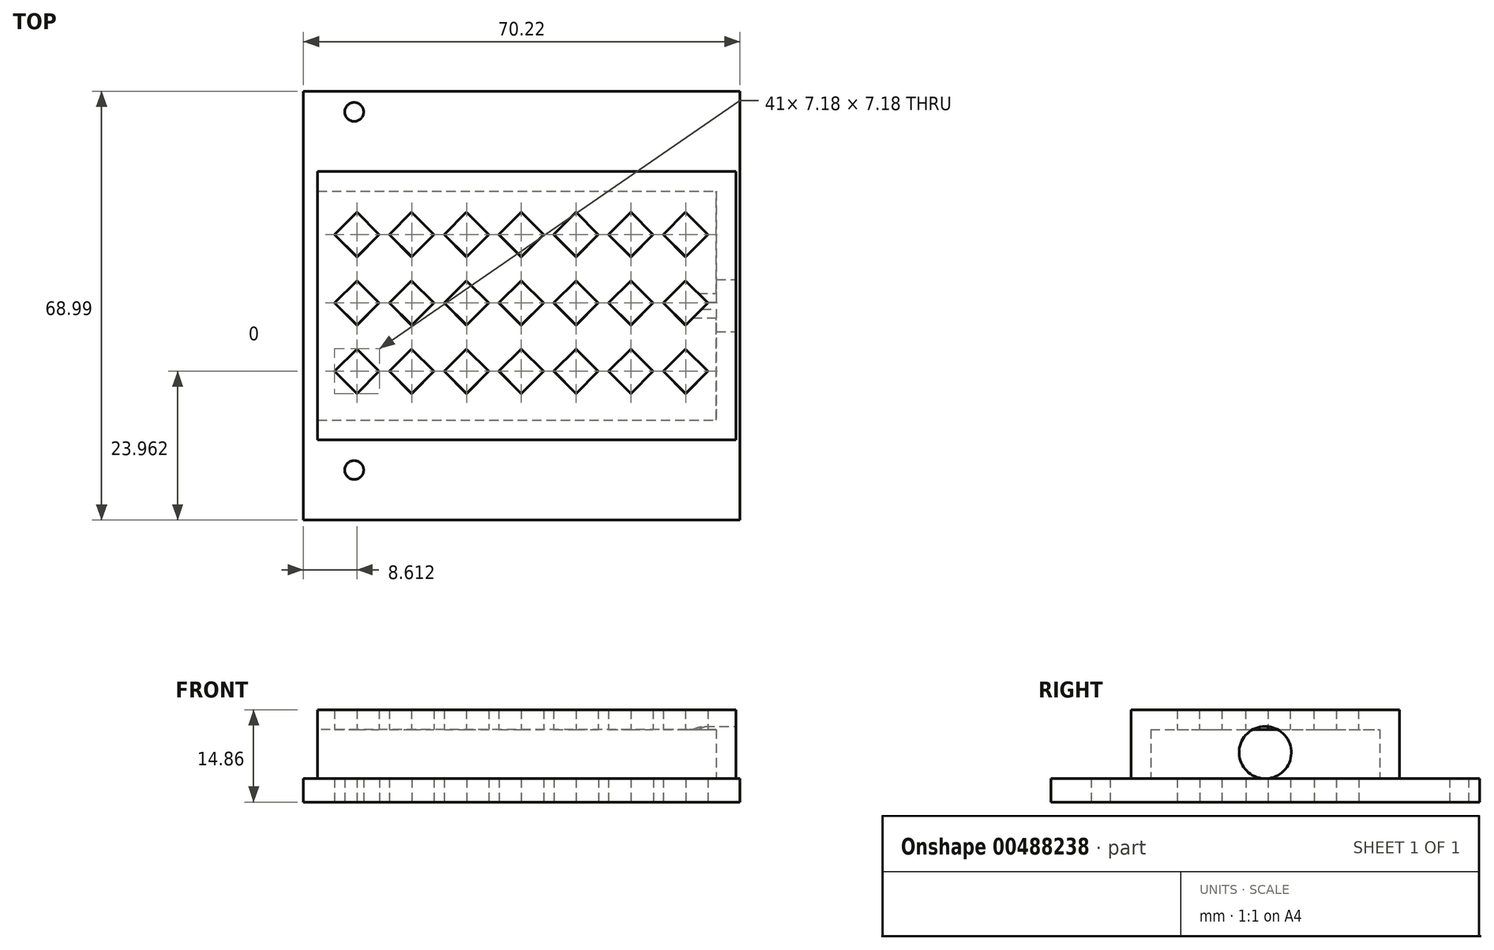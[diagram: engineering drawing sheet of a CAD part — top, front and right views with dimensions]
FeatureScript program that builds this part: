
annotation { "Feature Type Name" : "Feature", "Feature Type Description" : "" }
export const myFeature = defineFeature(function(context is Context, id is Id, definition is map)
    precondition{}
    {
        {
            var Q0;
            Q0=qCreatedBy(makeId("Top.planeOp"),FACE);
            var sketch = newSketch(context, id + "F0", { "sketchPlane" : qUnion([Q0])});
            skLineSegment(sketch, "E0.bottom", {"start": v(-28.53, -73.7) * mm, "end": v(41.7, -73.7) * mm});
            skLineSegment(sketch, "E0.top", {"start": v(-28.53, -4.71) * mm, "end": v(41.7, -4.71) * mm});
            skLineSegment(sketch, "E0.right", {"start": v(41.7, -73.7) * mm, "end": v(41.7, -4.71) * mm});
            skCircle(sketch, "E1", {"center": v(-20.37, -65.65) * mm, "radius": 1.52 * mm});
            skCircle(sketch, "E2.MirrorC", {"center": v(-20.37, -8.04) * mm, "radius": 1.52 * mm});
            skLineSegment(sketch, "E3", {"start": v(-28.53, -73.7) * mm, "end": v(-28.53, -4.71) * mm});
            skPoint(sketch, "E0.left.start.orphan", {"position": v(-40.99, -73.7) * mm});
            skLineSegment(sketch, "E4.bottom", {"start": v(37.9, -57.62) * mm, "end": v(-23.07, -57.62) * mm});
            skLineSegment(sketch, "E4.top", {"start": v(37.9, -20.8) * mm, "end": v(-23.07, -20.8) * mm});
            skLineSegment(sketch, "E4.left", {"start": v(37.9, -57.62) * mm, "end": v(37.9, -20.8) * mm});
            skPoint(sketch, "E4.middle", {"position": v(-28.53, -39.2) * mm});
            skLineSegment(sketch, "E5.0", {"start": v(41.07, -17.62) * mm, "end": v(-26.24, -17.62) * mm});
            skLineSegment(sketch, "E5.1", {"start": v(41.07, -60.8) * mm, "end": v(41.07, -17.62) * mm});
            skLineSegment(sketch, "E5.2", {"start": v(41.07, -60.8) * mm, "end": v(-26.24, -60.8) * mm});
            skLineSegment(sketch, "E5.3", {"start": v(-26.24, -60.8) * mm, "end": v(-26.24, -57.62) * mm});
            skLineSegment(sketch, "E6", {"start": v(-23.07, -20.8) * mm, "end": v(-26.24, -20.8) * mm});
            skLineSegment(sketch, "E7", {"start": v(-23.07, -57.62) * mm, "end": v(-26.24, -57.62) * mm});
            skLineSegment(sketch, "E8.trimOffspring", {"start": v(-26.24, -20.8) * mm, "end": v(-26.24, -17.62) * mm});
            skLineSegment(sketch, "E9.bottom", {"start": v(-19.92, -53.33) * mm, "end": v(-16.33, -49.74) * mm});
            skLineSegment(sketch, "E9.top", {"start": v(-23.5, -49.74) * mm, "end": v(-19.92, -46.15) * mm});
            skLineSegment(sketch, "E9.left", {"start": v(-19.92, -53.33) * mm, "end": v(-23.5, -49.74) * mm});
            skLineSegment(sketch, "E9.right", {"start": v(-16.33, -49.74) * mm, "end": v(-19.92, -46.15) * mm});
            skLineSegment(sketch, "E10.0.1.0", {"start": v(-19.92, -42.33) * mm, "end": v(-23.5, -38.74) * mm});
            skLineSegment(sketch, "E10.0.1.1", {"start": v(-19.92, -42.33) * mm, "end": v(-16.33, -38.74) * mm});
            skLineSegment(sketch, "E10.0.1.2", {"start": v(-16.33, -38.74) * mm, "end": v(-19.92, -35.15) * mm});
            skLineSegment(sketch, "E10.0.1.3", {"start": v(-23.5, -38.74) * mm, "end": v(-19.92, -35.15) * mm});
            skLineSegment(sketch, "E10.0.2.0", {"start": v(-19.92, -31.33) * mm, "end": v(-23.5, -27.74) * mm});
            skLineSegment(sketch, "E10.0.2.1", {"start": v(-19.92, -31.33) * mm, "end": v(-16.33, -27.74) * mm});
            skLineSegment(sketch, "E10.0.2.2", {"start": v(-16.33, -27.74) * mm, "end": v(-19.92, -24.15) * mm});
            skLineSegment(sketch, "E10.0.2.3", {"start": v(-23.5, -27.74) * mm, "end": v(-19.92, -24.15) * mm});
            skLineSegment(sketch, "E10.1.0.0", {"start": v(-11.1, -53.33) * mm, "end": v(-14.7, -49.74) * mm});
            skLineSegment(sketch, "E10.1.0.1", {"start": v(-11.1, -53.33) * mm, "end": v(-7.51, -49.74) * mm});
            skLineSegment(sketch, "E10.1.0.2", {"start": v(-7.51, -49.74) * mm, "end": v(-11.1, -46.15) * mm});
            skLineSegment(sketch, "E10.1.0.3", {"start": v(-14.7, -49.74) * mm, "end": v(-11.1, -46.15) * mm});
            skLineSegment(sketch, "E10.1.1.0", {"start": v(-11.1, -42.33) * mm, "end": v(-14.7, -38.74) * mm});
            skLineSegment(sketch, "E10.1.1.1", {"start": v(-11.1, -42.33) * mm, "end": v(-7.51, -38.74) * mm});
            skLineSegment(sketch, "E10.1.1.2", {"start": v(-7.51, -38.74) * mm, "end": v(-11.1, -35.15) * mm});
            skLineSegment(sketch, "E10.1.1.3", {"start": v(-14.7, -38.74) * mm, "end": v(-11.1, -35.15) * mm});
            skLineSegment(sketch, "E10.1.2.0", {"start": v(-11.1, -31.33) * mm, "end": v(-14.7, -27.74) * mm});
            skLineSegment(sketch, "E10.1.2.1", {"start": v(-11.1, -31.33) * mm, "end": v(-7.51, -27.74) * mm});
            skLineSegment(sketch, "E10.1.2.2", {"start": v(-7.51, -27.74) * mm, "end": v(-11.1, -24.15) * mm});
            skLineSegment(sketch, "E10.1.2.3", {"start": v(-14.7, -27.74) * mm, "end": v(-11.1, -24.15) * mm});
            skLineSegment(sketch, "E10.2.0.0", {"start": v(-2.3, -53.33) * mm, "end": v(-5.88, -49.74) * mm});
            skLineSegment(sketch, "E10.2.0.1", {"start": v(-2.3, -53.33) * mm, "end": v(1.3, -49.74) * mm});
            skLineSegment(sketch, "E10.2.0.2", {"start": v(1.3, -49.74) * mm, "end": v(-2.3, -46.15) * mm});
            skLineSegment(sketch, "E10.2.0.3", {"start": v(-5.88, -49.74) * mm, "end": v(-2.3, -46.15) * mm});
            skLineSegment(sketch, "E10.2.1.0", {"start": v(-2.3, -42.33) * mm, "end": v(-5.88, -38.74) * mm});
            skLineSegment(sketch, "E10.2.1.1", {"start": v(-2.3, -42.33) * mm, "end": v(1.3, -38.74) * mm});
            skLineSegment(sketch, "E10.2.1.2", {"start": v(1.3, -38.74) * mm, "end": v(-2.3, -35.15) * mm});
            skLineSegment(sketch, "E10.2.1.3", {"start": v(-5.88, -38.74) * mm, "end": v(-2.3, -35.15) * mm});
            skLineSegment(sketch, "E10.2.2.0", {"start": v(-2.3, -31.33) * mm, "end": v(-5.88, -27.74) * mm});
            skLineSegment(sketch, "E10.2.2.1", {"start": v(-2.3, -31.33) * mm, "end": v(1.3, -27.74) * mm});
            skLineSegment(sketch, "E10.2.2.2", {"start": v(1.3, -27.74) * mm, "end": v(-2.3, -24.15) * mm});
            skLineSegment(sketch, "E10.2.2.3", {"start": v(-5.88, -27.74) * mm, "end": v(-2.3, -24.15) * mm});
            skLineSegment(sketch, "E10.3.0.0", {"start": v(6.52, -53.33) * mm, "end": v(2.93, -49.74) * mm});
            skLineSegment(sketch, "E10.3.0.1", {"start": v(6.52, -53.33) * mm, "end": v(10.12, -49.74) * mm});
            skLineSegment(sketch, "E10.3.0.2", {"start": v(10.12, -49.74) * mm, "end": v(6.52, -46.15) * mm});
            skLineSegment(sketch, "E10.3.0.3", {"start": v(2.93, -49.74) * mm, "end": v(6.52, -46.15) * mm});
            skLineSegment(sketch, "E10.3.1.0", {"start": v(6.52, -42.33) * mm, "end": v(2.93, -38.74) * mm});
            skLineSegment(sketch, "E10.3.1.1", {"start": v(6.52, -42.33) * mm, "end": v(10.12, -38.74) * mm});
            skLineSegment(sketch, "E10.3.1.2", {"start": v(10.12, -38.74) * mm, "end": v(6.52, -35.15) * mm});
            skLineSegment(sketch, "E10.3.1.3", {"start": v(2.93, -38.74) * mm, "end": v(6.52, -35.15) * mm});
            skLineSegment(sketch, "E10.3.2.0", {"start": v(6.52, -31.33) * mm, "end": v(2.93, -27.74) * mm});
            skLineSegment(sketch, "E10.3.2.1", {"start": v(6.52, -31.33) * mm, "end": v(10.12, -27.74) * mm});
            skLineSegment(sketch, "E10.3.2.2", {"start": v(10.12, -27.74) * mm, "end": v(6.52, -24.15) * mm});
            skLineSegment(sketch, "E10.3.2.3", {"start": v(2.93, -27.74) * mm, "end": v(6.52, -24.15) * mm});
            skLineSegment(sketch, "E10.4.0.0", {"start": v(15.34, -53.33) * mm, "end": v(11.75, -49.74) * mm});
            skLineSegment(sketch, "E10.4.0.1", {"start": v(15.34, -53.33) * mm, "end": v(18.93, -49.74) * mm});
            skLineSegment(sketch, "E10.4.0.2", {"start": v(18.93, -49.74) * mm, "end": v(15.34, -46.15) * mm});
            skLineSegment(sketch, "E10.4.0.3", {"start": v(11.75, -49.74) * mm, "end": v(15.34, -46.15) * mm});
            skLineSegment(sketch, "E10.4.1.0", {"start": v(15.34, -42.33) * mm, "end": v(11.75, -38.74) * mm});
            skLineSegment(sketch, "E10.4.1.1", {"start": v(15.34, -42.33) * mm, "end": v(18.93, -38.74) * mm});
            skLineSegment(sketch, "E10.4.1.2", {"start": v(18.93, -38.74) * mm, "end": v(15.34, -35.15) * mm});
            skLineSegment(sketch, "E10.4.1.3", {"start": v(11.75, -38.74) * mm, "end": v(15.34, -35.15) * mm});
            skLineSegment(sketch, "E10.4.2.0", {"start": v(15.34, -31.33) * mm, "end": v(11.75, -27.74) * mm});
            skLineSegment(sketch, "E10.4.2.1", {"start": v(15.34, -31.33) * mm, "end": v(18.93, -27.74) * mm});
            skLineSegment(sketch, "E10.4.2.2", {"start": v(18.93, -27.74) * mm, "end": v(15.34, -24.15) * mm});
            skLineSegment(sketch, "E10.4.2.3", {"start": v(11.75, -27.74) * mm, "end": v(15.34, -24.15) * mm});
            skLineSegment(sketch, "E10.5.0.0", {"start": v(24.15, -53.33) * mm, "end": v(20.56, -49.74) * mm});
            skLineSegment(sketch, "E10.5.0.1", {"start": v(24.15, -53.33) * mm, "end": v(27.74, -49.74) * mm});
            skLineSegment(sketch, "E10.5.0.2", {"start": v(27.74, -49.74) * mm, "end": v(24.15, -46.15) * mm});
            skLineSegment(sketch, "E10.5.0.3", {"start": v(20.56, -49.74) * mm, "end": v(24.15, -46.15) * mm});
            skLineSegment(sketch, "E10.5.1.0", {"start": v(24.15, -42.33) * mm, "end": v(20.56, -38.74) * mm});
            skLineSegment(sketch, "E10.5.1.1", {"start": v(24.15, -42.33) * mm, "end": v(27.74, -38.74) * mm});
            skLineSegment(sketch, "E10.5.1.2", {"start": v(27.74, -38.74) * mm, "end": v(24.15, -35.15) * mm});
            skLineSegment(sketch, "E10.5.1.3", {"start": v(20.56, -38.74) * mm, "end": v(24.15, -35.15) * mm});
            skLineSegment(sketch, "E10.5.2.0", {"start": v(24.15, -31.33) * mm, "end": v(20.56, -27.74) * mm});
            skLineSegment(sketch, "E10.5.2.1", {"start": v(24.15, -31.33) * mm, "end": v(27.74, -27.74) * mm});
            skLineSegment(sketch, "E10.5.2.2", {"start": v(27.74, -27.74) * mm, "end": v(24.15, -24.15) * mm});
            skLineSegment(sketch, "E10.5.2.3", {"start": v(20.56, -27.74) * mm, "end": v(24.15, -24.15) * mm});
            skLineSegment(sketch, "E10.6.0.0", {"start": v(32.96, -53.33) * mm, "end": v(29.37, -49.74) * mm});
            skLineSegment(sketch, "E10.6.0.1", {"start": v(32.96, -53.33) * mm, "end": v(36.56, -49.74) * mm});
            skLineSegment(sketch, "E10.6.0.2", {"start": v(36.56, -49.74) * mm, "end": v(32.96, -46.15) * mm});
            skLineSegment(sketch, "E10.6.0.3", {"start": v(29.37, -49.74) * mm, "end": v(32.96, -46.15) * mm});
            skLineSegment(sketch, "E10.6.1.0", {"start": v(32.96, -42.33) * mm, "end": v(29.37, -38.74) * mm});
            skLineSegment(sketch, "E10.6.1.1", {"start": v(32.96, -42.33) * mm, "end": v(36.56, -38.74) * mm});
            skLineSegment(sketch, "E10.6.1.2", {"start": v(36.56, -38.74) * mm, "end": v(32.96, -35.15) * mm});
            skLineSegment(sketch, "E10.6.1.3", {"start": v(29.37, -38.74) * mm, "end": v(32.96, -35.15) * mm});
            skLineSegment(sketch, "E10.6.2.0", {"start": v(32.96, -31.33) * mm, "end": v(29.37, -27.74) * mm});
            skLineSegment(sketch, "E10.6.2.1", {"start": v(32.96, -31.33) * mm, "end": v(36.56, -27.74) * mm});
            skLineSegment(sketch, "E10.6.2.2", {"start": v(36.56, -27.74) * mm, "end": v(32.96, -24.15) * mm});
            skLineSegment(sketch, "E10.6.2.3", {"start": v(29.37, -27.74) * mm, "end": v(32.96, -24.15) * mm});
            skLineSegment(sketch, "E10.direction1", {"start": v(-19.92, -53.33) * mm, "end": v(-11.1, -53.33) * mm, "construction": true});
            skLineSegment(sketch, "E10.direction2", {"start": v(-19.92, -53.33) * mm, "end": v(-19.92, -42.33) * mm, "construction": true});
            skSolve(sketch);
        }
        {
            var Q0;
            Q0=makeQuery(id+"F0.imprint","IMPRINT",FACE,{"disambiguationData":[TD([[makeQuery(id+"F0.imprint","IMPRINT",EDGE,{"derivedFrom":sQuery(id+"F0.wireOp",EDGE,"E0.bottom")}),1.0]])]});
            var Q1;
            Q1=makeQuery(id+"F0.imprint","IMPRINT",FACE,{"disambiguationData":[TD([[makeQuery(id+"F0.imprint","IMPRINT",EDGE,{"derivedFrom":sQuery(id+"F0.wireOp",EDGE,"E4.bottom")}),1.0]])]});
            extrude(context, id + "F1", {"entities" : qUnion([Q0, Q1]), "depth" : 3.8 * mm, "offsetDistance" : 25.4 * mm});
        }
        {
            var Q0;
            Q0=makeQuery(id+"F0.imprint","IMPRINT",FACE,{"disambiguationData":[TD([[makeQuery(id+"F0.imprint","IMPRINT",EDGE,{"derivedFrom":sQuery(id+"F0.wireOp",EDGE,"E4.bottom")}),1.0]])]});
            extrude(context, id + "F2", {"entities" : qUnion([Q0]), "operationType" : NewBodyOperationType.ADD, "depth" : 11.68 * mm, "offsetDistance" : 25.4 * mm});
        }
        {
            var Q0;
            Q0=makeQuery(id+"F2.opExtrude","CAP_FACE",FACE,{"disambiguationData":[OSD([sQuery(id+"F0.wireOp",EDGE,"E4.bottom"),sQuery(id+"F0.wireOp",EDGE,"E4.top"),sQuery(id+"F0.wireOp",EDGE,"E4.left"),sQuery(id+"F0.wireOp",EDGE,"E5.0"),sQuery(id+"F0.wireOp",EDGE,"E5.1"),sQuery(id+"F0.wireOp",EDGE,"E5.2"),sQuery(id+"F0.wireOp",EDGE,"E5.3"),sQuery(id+"F0.wireOp",EDGE,"E6"),sQuery(id+"F0.wireOp",EDGE,"E7"),sQuery(id+"F0.wireOp",EDGE,"E8.trimOffspring")])],"isStart":false});
            var sketch = newSketch(context, id + "F3", { "sketchPlane" : qUnion([Q0])});
            skLineSegment(sketch, "E11.bottom", {"start": v(-26.24, -60.8) * mm, "end": v(41.07, -60.8) * mm});
            skLineSegment(sketch, "E11.top", {"start": v(-26.24, -17.62) * mm, "end": v(41.07, -17.62) * mm});
            skLineSegment(sketch, "E11.left", {"start": v(-26.24, -60.8) * mm, "end": v(-26.24, -17.62) * mm});
            skLineSegment(sketch, "E11.right", {"start": v(41.07, -60.8) * mm, "end": v(41.07, -17.62) * mm});
            skPoint(sketch, "E12.middle", {"position": v(-28.56, -39.24) * mm});
            skLineSegment(sketch, "E13.bottom", {"start": v(-19.94, -53.36) * mm, "end": v(-16.35, -49.77) * mm});
            skLineSegment(sketch, "E13.top", {"start": v(-23.54, -49.77) * mm, "end": v(-19.94, -46.17) * mm});
            skLineSegment(sketch, "E13.left", {"start": v(-19.94, -53.36) * mm, "end": v(-23.54, -49.77) * mm});
            skLineSegment(sketch, "E13.right", {"start": v(-16.35, -49.77) * mm, "end": v(-19.94, -46.17) * mm});
            skLineSegment(sketch, "E14.0.1.0", {"start": v(-19.94, -42.36) * mm, "end": v(-23.54, -38.77) * mm});
            skLineSegment(sketch, "E14.0.1.1", {"start": v(-19.94, -42.36) * mm, "end": v(-16.35, -38.77) * mm});
            skLineSegment(sketch, "E14.0.1.2", {"start": v(-16.35, -38.77) * mm, "end": v(-19.94, -35.18) * mm});
            skLineSegment(sketch, "E14.0.1.3", {"start": v(-23.54, -38.77) * mm, "end": v(-19.94, -35.18) * mm});
            skLineSegment(sketch, "E14.0.2.0", {"start": v(-19.94, -31.36) * mm, "end": v(-23.54, -27.77) * mm});
            skLineSegment(sketch, "E14.0.2.1", {"start": v(-19.94, -31.36) * mm, "end": v(-16.35, -27.77) * mm});
            skLineSegment(sketch, "E14.0.2.2", {"start": v(-16.35, -27.77) * mm, "end": v(-19.94, -24.18) * mm});
            skLineSegment(sketch, "E14.0.2.3", {"start": v(-23.54, -27.77) * mm, "end": v(-19.94, -24.18) * mm});
            skLineSegment(sketch, "E14.1.0.0", {"start": v(-11.13, -53.36) * mm, "end": v(-14.72, -49.77) * mm});
            skLineSegment(sketch, "E14.1.0.1", {"start": v(-11.13, -53.36) * mm, "end": v(-7.54, -49.77) * mm});
            skLineSegment(sketch, "E14.1.0.2", {"start": v(-7.54, -49.77) * mm, "end": v(-11.13, -46.17) * mm});
            skLineSegment(sketch, "E14.1.0.3", {"start": v(-14.72, -49.77) * mm, "end": v(-11.13, -46.17) * mm});
            skLineSegment(sketch, "E14.1.1.0", {"start": v(-11.13, -42.36) * mm, "end": v(-14.72, -38.77) * mm});
            skLineSegment(sketch, "E14.1.1.1", {"start": v(-11.13, -42.36) * mm, "end": v(-7.54, -38.77) * mm});
            skLineSegment(sketch, "E14.1.1.2", {"start": v(-7.54, -38.77) * mm, "end": v(-11.13, -35.18) * mm});
            skLineSegment(sketch, "E14.1.1.3", {"start": v(-14.72, -38.77) * mm, "end": v(-11.13, -35.18) * mm});
            skLineSegment(sketch, "E14.1.2.0", {"start": v(-11.13, -31.36) * mm, "end": v(-14.72, -27.77) * mm});
            skLineSegment(sketch, "E14.1.2.1", {"start": v(-11.13, -31.36) * mm, "end": v(-7.54, -27.77) * mm});
            skLineSegment(sketch, "E14.1.2.2", {"start": v(-7.54, -27.77) * mm, "end": v(-11.13, -24.18) * mm});
            skLineSegment(sketch, "E14.1.2.3", {"start": v(-14.72, -27.77) * mm, "end": v(-11.13, -24.18) * mm});
            skLineSegment(sketch, "E14.2.0.0", {"start": v(-2.32, -53.36) * mm, "end": v(-5.9, -49.77) * mm});
            skLineSegment(sketch, "E14.2.0.1", {"start": v(-2.32, -53.36) * mm, "end": v(1.28, -49.77) * mm});
            skLineSegment(sketch, "E14.2.0.2", {"start": v(1.28, -49.77) * mm, "end": v(-2.32, -46.17) * mm});
            skLineSegment(sketch, "E14.2.0.3", {"start": v(-5.9, -49.77) * mm, "end": v(-2.32, -46.17) * mm});
            skLineSegment(sketch, "E14.2.1.0", {"start": v(-2.32, -42.36) * mm, "end": v(-5.9, -38.77) * mm});
            skLineSegment(sketch, "E14.2.1.1", {"start": v(-2.32, -42.36) * mm, "end": v(1.28, -38.77) * mm});
            skLineSegment(sketch, "E14.2.1.2", {"start": v(1.28, -38.77) * mm, "end": v(-2.32, -35.18) * mm});
            skLineSegment(sketch, "E14.2.1.3", {"start": v(-5.9, -38.77) * mm, "end": v(-2.32, -35.18) * mm});
            skLineSegment(sketch, "E14.2.2.0", {"start": v(-2.32, -31.36) * mm, "end": v(-5.9, -27.77) * mm});
            skLineSegment(sketch, "E14.2.2.1", {"start": v(-2.32, -31.36) * mm, "end": v(1.28, -27.77) * mm});
            skLineSegment(sketch, "E14.2.2.2", {"start": v(1.28, -27.77) * mm, "end": v(-2.32, -24.18) * mm});
            skLineSegment(sketch, "E14.2.2.3", {"start": v(-5.9, -27.77) * mm, "end": v(-2.32, -24.18) * mm});
            skLineSegment(sketch, "E14.3.0.0", {"start": v(6.5, -53.36) * mm, "end": v(2.9, -49.77) * mm});
            skLineSegment(sketch, "E14.3.0.1", {"start": v(6.5, -53.36) * mm, "end": v(10.09, -49.77) * mm});
            skLineSegment(sketch, "E14.3.0.2", {"start": v(10.09, -49.77) * mm, "end": v(6.5, -46.17) * mm});
            skLineSegment(sketch, "E14.3.0.3", {"start": v(2.9, -49.77) * mm, "end": v(6.5, -46.17) * mm});
            skLineSegment(sketch, "E14.3.1.0", {"start": v(6.5, -42.36) * mm, "end": v(2.9, -38.77) * mm});
            skLineSegment(sketch, "E14.3.1.1", {"start": v(6.5, -42.36) * mm, "end": v(10.09, -38.77) * mm});
            skLineSegment(sketch, "E14.3.1.2", {"start": v(10.09, -38.77) * mm, "end": v(6.5, -35.18) * mm});
            skLineSegment(sketch, "E14.3.1.3", {"start": v(2.9, -38.77) * mm, "end": v(6.5, -35.18) * mm});
            skLineSegment(sketch, "E14.3.2.0", {"start": v(6.5, -31.36) * mm, "end": v(2.9, -27.77) * mm});
            skLineSegment(sketch, "E14.3.2.1", {"start": v(6.5, -31.36) * mm, "end": v(10.09, -27.77) * mm});
            skLineSegment(sketch, "E14.3.2.2", {"start": v(10.09, -27.77) * mm, "end": v(6.5, -24.18) * mm});
            skLineSegment(sketch, "E14.3.2.3", {"start": v(2.9, -27.77) * mm, "end": v(6.5, -24.18) * mm});
            skLineSegment(sketch, "E14.4.0.0", {"start": v(15.31, -53.36) * mm, "end": v(11.72, -49.77) * mm});
            skLineSegment(sketch, "E14.4.0.1", {"start": v(15.31, -53.36) * mm, "end": v(18.9, -49.77) * mm});
            skLineSegment(sketch, "E14.4.0.2", {"start": v(18.9, -49.77) * mm, "end": v(15.31, -46.17) * mm});
            skLineSegment(sketch, "E14.4.0.3", {"start": v(11.72, -49.77) * mm, "end": v(15.31, -46.17) * mm});
            skLineSegment(sketch, "E14.4.1.0", {"start": v(15.31, -42.36) * mm, "end": v(11.72, -38.77) * mm});
            skLineSegment(sketch, "E14.4.1.1", {"start": v(15.31, -42.36) * mm, "end": v(18.9, -38.77) * mm});
            skLineSegment(sketch, "E14.4.1.2", {"start": v(18.9, -38.77) * mm, "end": v(15.31, -35.18) * mm});
            skLineSegment(sketch, "E14.4.1.3", {"start": v(11.72, -38.77) * mm, "end": v(15.31, -35.18) * mm});
            skLineSegment(sketch, "E14.4.2.0", {"start": v(15.31, -31.36) * mm, "end": v(11.72, -27.77) * mm});
            skLineSegment(sketch, "E14.4.2.1", {"start": v(15.31, -31.36) * mm, "end": v(18.9, -27.77) * mm});
            skLineSegment(sketch, "E14.4.2.2", {"start": v(18.9, -27.77) * mm, "end": v(15.31, -24.18) * mm});
            skLineSegment(sketch, "E14.4.2.3", {"start": v(11.72, -27.77) * mm, "end": v(15.31, -24.18) * mm});
            skLineSegment(sketch, "E14.5.0.0", {"start": v(24.13, -53.36) * mm, "end": v(20.53, -49.77) * mm});
            skLineSegment(sketch, "E14.5.0.1", {"start": v(24.13, -53.36) * mm, "end": v(27.72, -49.77) * mm});
            skLineSegment(sketch, "E14.5.0.2", {"start": v(27.72, -49.77) * mm, "end": v(24.13, -46.17) * mm});
            skLineSegment(sketch, "E14.5.0.3", {"start": v(20.53, -49.77) * mm, "end": v(24.13, -46.17) * mm});
            skLineSegment(sketch, "E14.5.1.0", {"start": v(24.13, -42.36) * mm, "end": v(20.53, -38.77) * mm});
            skLineSegment(sketch, "E14.5.1.1", {"start": v(24.13, -42.36) * mm, "end": v(27.72, -38.77) * mm});
            skLineSegment(sketch, "E14.5.1.2", {"start": v(27.72, -38.77) * mm, "end": v(24.13, -35.18) * mm});
            skLineSegment(sketch, "E14.5.1.3", {"start": v(20.53, -38.77) * mm, "end": v(24.13, -35.18) * mm});
            skLineSegment(sketch, "E14.5.2.0", {"start": v(24.13, -31.36) * mm, "end": v(20.53, -27.77) * mm});
            skLineSegment(sketch, "E14.5.2.1", {"start": v(24.13, -31.36) * mm, "end": v(27.72, -27.77) * mm});
            skLineSegment(sketch, "E14.5.2.2", {"start": v(27.72, -27.77) * mm, "end": v(24.13, -24.18) * mm});
            skLineSegment(sketch, "E14.5.2.3", {"start": v(20.53, -27.77) * mm, "end": v(24.13, -24.18) * mm});
            skLineSegment(sketch, "E14.6.0.0", {"start": v(32.94, -53.36) * mm, "end": v(29.35, -49.77) * mm});
            skLineSegment(sketch, "E14.6.0.1", {"start": v(32.94, -53.36) * mm, "end": v(36.53, -49.77) * mm});
            skLineSegment(sketch, "E14.6.0.2", {"start": v(36.53, -49.77) * mm, "end": v(32.94, -46.17) * mm});
            skLineSegment(sketch, "E14.6.0.3", {"start": v(29.35, -49.77) * mm, "end": v(32.94, -46.17) * mm});
            skLineSegment(sketch, "E14.6.1.0", {"start": v(32.94, -42.36) * mm, "end": v(29.35, -38.77) * mm});
            skLineSegment(sketch, "E14.6.1.1", {"start": v(32.94, -42.36) * mm, "end": v(36.53, -38.77) * mm});
            skLineSegment(sketch, "E14.6.1.2", {"start": v(36.53, -38.77) * mm, "end": v(32.94, -35.18) * mm});
            skLineSegment(sketch, "E14.6.1.3", {"start": v(29.35, -38.77) * mm, "end": v(32.94, -35.18) * mm});
            skLineSegment(sketch, "E14.6.2.0", {"start": v(32.94, -31.36) * mm, "end": v(29.35, -27.77) * mm});
            skLineSegment(sketch, "E14.6.2.1", {"start": v(32.94, -31.36) * mm, "end": v(36.53, -27.77) * mm});
            skLineSegment(sketch, "E14.6.2.2", {"start": v(36.53, -27.77) * mm, "end": v(32.94, -24.18) * mm});
            skLineSegment(sketch, "E14.6.2.3", {"start": v(29.35, -27.77) * mm, "end": v(32.94, -24.18) * mm});
            skLineSegment(sketch, "E14.direction1", {"start": v(-19.94, -53.36) * mm, "end": v(-11.13, -53.36) * mm, "construction": true});
            skLineSegment(sketch, "E14.direction2", {"start": v(-19.94, -53.36) * mm, "end": v(-19.94, -42.36) * mm, "construction": true});
            skSolve(sketch);
        }
        {
            var Q0;
            Q0 = qSketchRegion(id + "F3", true);
            extrude(context, id + "F4", {"entities" : qUnion([Q0]), "operationType" : NewBodyOperationType.ADD, "depth" : 3.17 * mm, "offsetDistance" : 25.4 * mm});
        }
        {
            var Q0;
            Q0=makeQuery(id+"F4.boolean.opBoolean","MERGE",FACE,{"derivedFrom":[makeQuery(id+"F2.opExtrude","SWEPT_FACE",FACE,{"disambiguationData":[OSD([sQuery(id+"F0.wireOp",EDGE,"E5.1")])]}),makeQuery(id+"F4.opExtrude","SWEPT_FACE",FACE,{"disambiguationData":[OSD([sQuery(id+"F3.wireOp",EDGE,"E11.right")])]})]});
            var sketch = newSketch(context, id + "F5", { "sketchPlane" : qUnion([Q0])});
            skCircle(sketch, "E15", {"center": v(-39.2, 7.98) * mm, "radius": 4.2 * mm});
            skPoint(sketch, "E15.centerSnap0", {"position": v(-39.2, 14.86) * mm});
            skSolve(sketch);
        }
        {
            var Q0;
            Q0 = qSketchRegion(id + "F5", true);
            extrude(context, id + "F6", {"entities" : qUnion([Q0]), "operationType" : NewBodyOperationType.REMOVE, "endBound" : BoundingType.UP_TO_NEXT, "oppositeDirection" : true, "depth" : 25.4 * mm, "offsetDistance" : 25.4 * mm});
        }
    });
